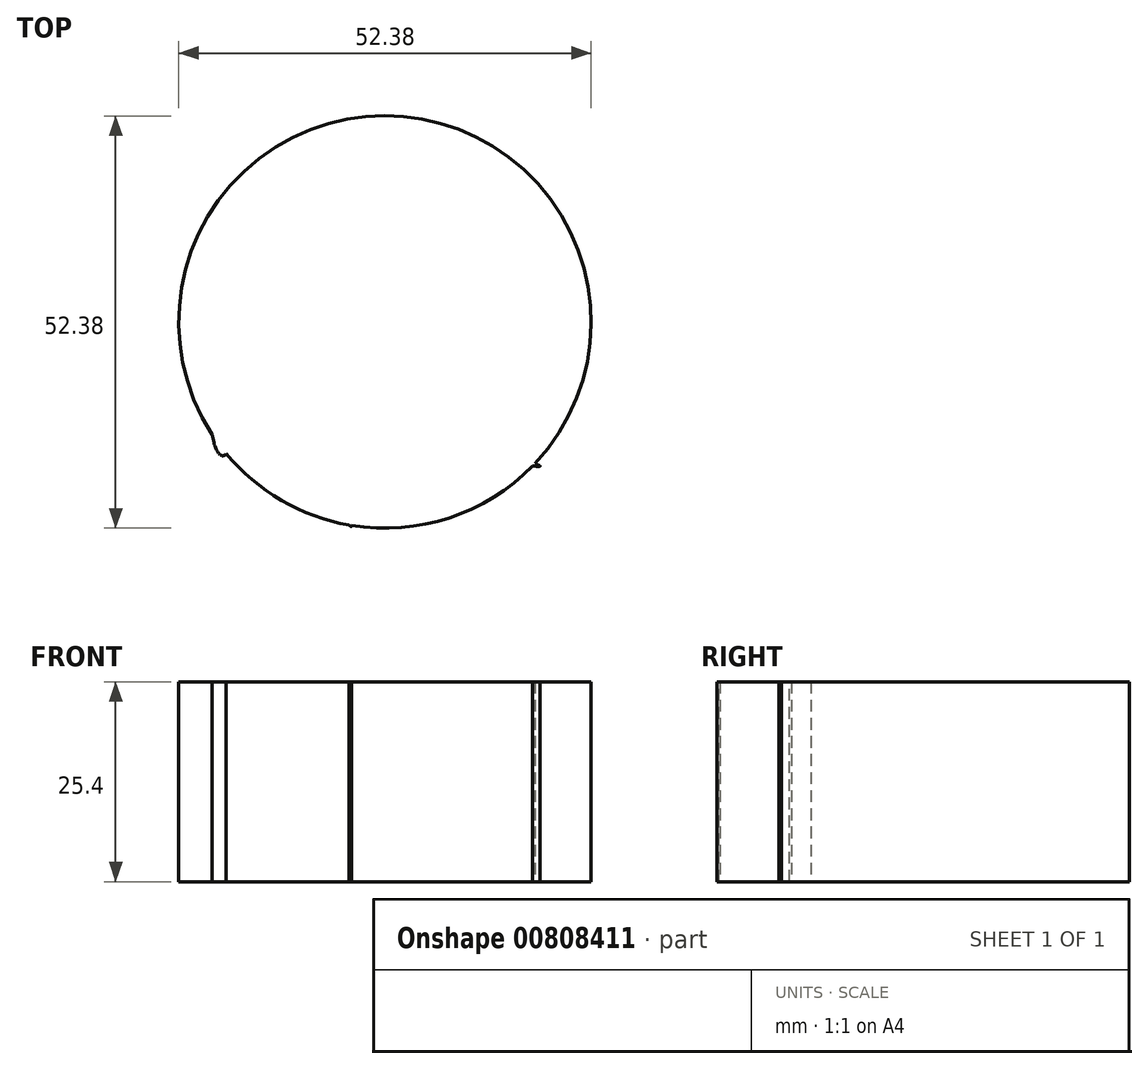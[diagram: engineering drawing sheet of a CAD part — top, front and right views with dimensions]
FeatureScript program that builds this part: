
annotation { "Feature Type Name" : "Feature", "Feature Type Description" : "" }
export const myFeature = defineFeature(function(context is Context, id is Id, definition is map)
    precondition{}
    {
        {
            var Q0;
            Q0=qCreatedBy(makeId("Top.planeOp"),FACE);
            var sketch = newSketch(context, id + "F0", { "sketchPlane" : qUnion([Q0])});
            skCircle(sketch, "E0", {"center": v(0, 0) * mm, "radius": 26.2 * mm});
            skSolve(sketch);
        }
        {
            var Q0;
            Q0=makeQuery(id+"F0.imprint","IMPRINT",FACE,{"disambiguationData":[TD([[makeQuery(id+"F0.imprint","IMPRINT",EDGE,{"derivedFrom":sQuery(id+"F0.wireOp",EDGE,"E0")}),1.0]])]});
            extrude(context, id + "F1", {"entities" : qUnion([Q0]), "depth" : 25.4 * mm, "offsetDistance" : 25.4 * mm});
        }
        {
            var Q0;
            Q0=qCreatedBy(makeId("Top.planeOp"),FACE);
            var sketch = newSketch(context, id + "F2", { "sketchPlane" : qUnion([Q0])});
            skLineSegment(sketch, "E1.bottom", {"start": v(-5.74, 5.74) * mm, "end": v(5.43, 5.74) * mm});
            skLineSegment(sketch, "E1.top", {"start": v(-5.74, -4.8) * mm, "end": v(5.43, -4.8) * mm});
            skLineSegment(sketch, "E1.left", {"start": v(-5.74, 5.74) * mm, "end": v(-5.74, -4.8) * mm});
            skLineSegment(sketch, "E1.right", {"start": v(5.43, 5.74) * mm, "end": v(5.43, -4.8) * mm});
            skFitSpline(sketch, "E2", {"points": [v(0, 5.74) * mm, v(0, 10.71) * mm, v(-10.98, 22.8) * mm, v(-3.42, 10.4) * mm, v(-5.74, 5.74) * mm, v(0, 5.74) * mm]});
            skFitSpline(sketch, "E3", {"points": [v(5.43, 0.47) * mm, v(9.27, 5.74) * mm, v(10.18, 23.4) * mm, v(5.43, 9.2) * mm, v(5.43, 0.47) * mm]});
            skFitSpline(sketch, "E4", {"points": [v(5.43, -4.8) * mm, v(9.88, -4.8) * mm, v(25.3, 0) * mm, v(9.58, 0) * mm, v(2.93, 0.47) * mm, v(5.43, -4.8) * mm]});
            skFitSpline(sketch, "E5", {"points": [v(-0.16, -4.8) * mm, v(0, -11.55) * mm, v(19.7, -18.29) * mm, v(3.23, -10.62) * mm, v(2.86, -4.8) * mm, v(-0.16, -4.8) * mm]});
            skFitSpline(sketch, "E6", {"points": [v(-5.74, -2.2) * mm, v(-11, -11) * mm, v(-4.26, -25.96) * mm, v(-8, -11.55) * mm, v(-3.13, -4.8) * mm, v(-5.74, -2.2) * mm]});
            skFitSpline(sketch, "E7", {"points": [v(-4.26, 3.8) * mm, v(-10.8, 3.8) * mm, v(-21.85, -10.43) * mm, v(-20.73, -16.98) * mm, v(-18.3, -12.67) * mm, v(-9.68, 0) * mm, v(-4.07, 0) * mm, v(-4.26, 3.8) * mm]});
            skSolve(sketch);
        }
        {
            var Q0;
            Q0 = qSketchRegion(id + "F2", true);
            extrude(context, id + "F3", {"entities" : qUnion([Q0]), "operationType" : NewBodyOperationType.ADD, "depth" : 25.4 * mm, "offsetDistance" : 25.4 * mm});
        }
    });
